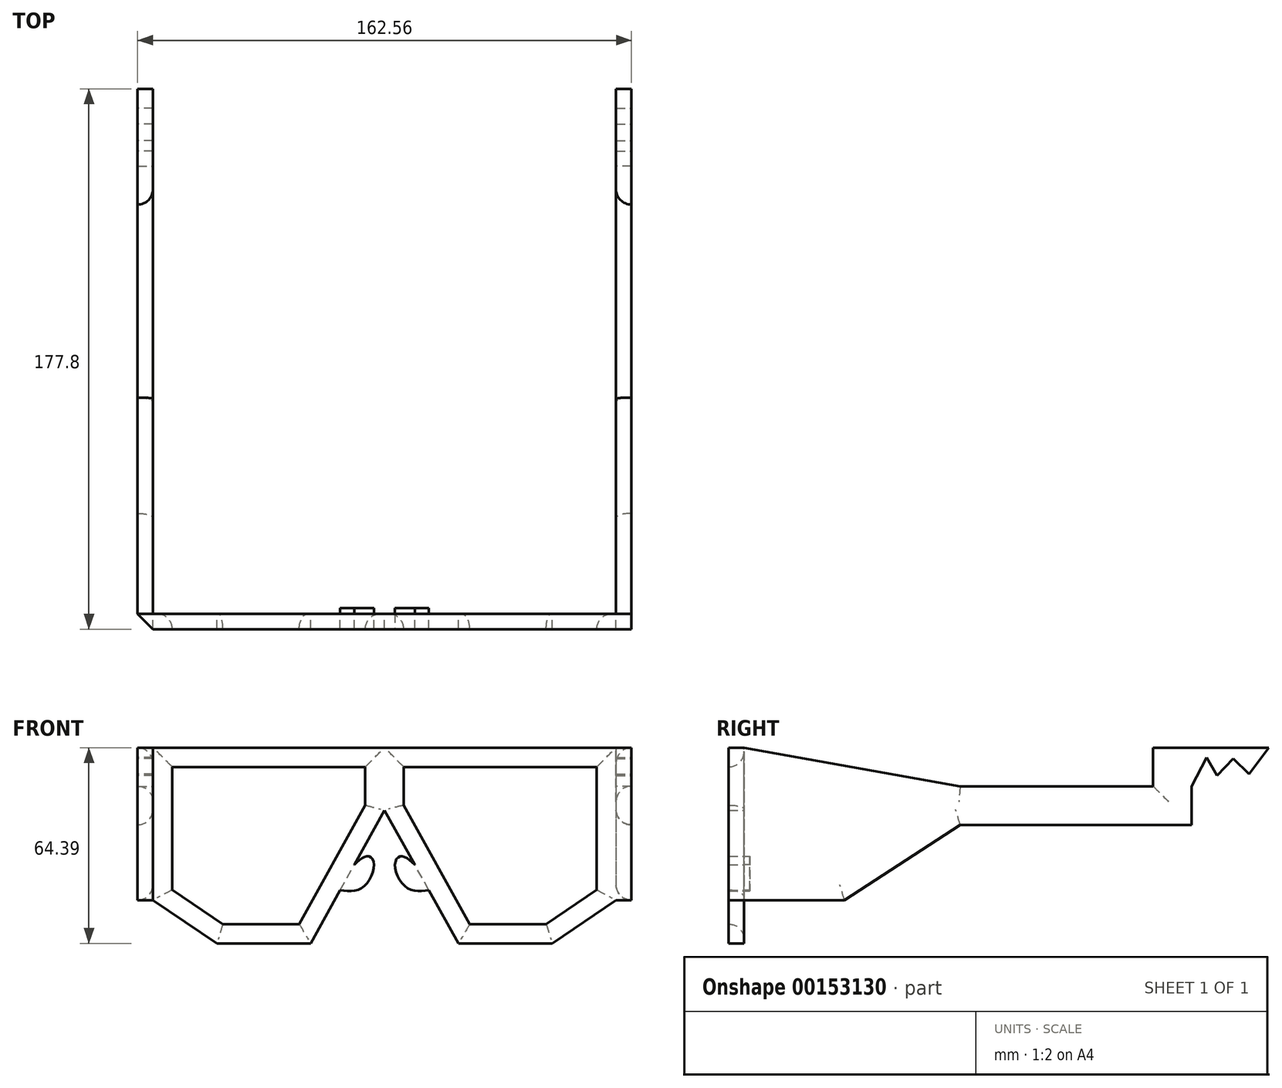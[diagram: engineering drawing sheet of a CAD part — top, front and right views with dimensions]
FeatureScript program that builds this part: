
annotation { "Feature Type Name" : "Feature", "Feature Type Description" : "" }
export const myFeature = defineFeature(function(context is Context, id is Id, definition is map)
    precondition{}
    {
        {
            var Q0;
            Q0=qCreatedBy(makeId("Front.planeOp"),FACE);
            var sketch = newSketch(context, id + "F0", { "sketchPlane" : qUnion([Q0])});
            skLineSegment(sketch, "E0", {"start": v(0, -20.57) * mm, "end": v(0, 0) * mm});
            skLineSegment(sketch, "E1", {"start": v(-76.2, 0) * mm, "end": v(-76.2, -50.16) * mm});
            skLineSegment(sketch, "E2", {"start": v(-76.2, -50.16) * mm, "end": v(-55.16, -64.4) * mm});
            skLineSegment(sketch, "E3", {"start": v(-55.16, -64.4) * mm, "end": v(-24.34, -64.4) * mm});
            skLineSegment(sketch, "E4", {"start": v(-24.34, -64.4) * mm, "end": v(0, -20.57) * mm});
            skLineSegment(sketch, "E5", {"start": v(-76.2, 0) * mm, "end": v(0, 0) * mm});
            skLineSegment(sketch, "E6.0", {"start": v(-53.22, -58.04) * mm, "end": v(-28.08, -58.04) * mm});
            skLineSegment(sketch, "E6.1", {"start": v(-6.35, -18.92) * mm, "end": v(-6.35, -6.35) * mm});
            skLineSegment(sketch, "E6.2", {"start": v(-69.85, -6.35) * mm, "end": v(-6.35, -6.35) * mm});
            skLineSegment(sketch, "E6.3", {"start": v(-28.08, -58.04) * mm, "end": v(-6.35, -18.92) * mm});
            skLineSegment(sketch, "E6.4", {"start": v(-69.85, -6.35) * mm, "end": v(-69.85, -46.79) * mm});
            skLineSegment(sketch, "E6.5", {"start": v(-69.85, -46.79) * mm, "end": v(-53.22, -58.04) * mm});
            skLineSegment(sketch, "E7.MirrorCS", {"start": v(69.85, -6.35) * mm, "end": v(6.35, -6.35) * mm});
            skLineSegment(sketch, "E8.MirrorCS", {"start": v(69.85, -46.79) * mm, "end": v(53.22, -58.04) * mm});
            skLineSegment(sketch, "E9.MirrorCS", {"start": v(24.34, -64.4) * mm, "end": v(0, -20.57) * mm});
            skLineSegment(sketch, "E10.MirrorCS", {"start": v(76.2, 0) * mm, "end": v(76.2, -50.16) * mm});
            skLineSegment(sketch, "E11.MirrorCS", {"start": v(28.08, -58.04) * mm, "end": v(6.35, -18.92) * mm});
            skLineSegment(sketch, "E12.MirrorCS", {"start": v(76.2, 0) * mm, "end": v(0, 0) * mm});
            skLineSegment(sketch, "E13.MirrorCS", {"start": v(6.35, -18.92) * mm, "end": v(6.35, -6.35) * mm});
            skLineSegment(sketch, "E14.MirrorCS", {"start": v(76.2, -50.16) * mm, "end": v(55.16, -64.4) * mm});
            skLineSegment(sketch, "E15.MirrorCS", {"start": v(53.22, -58.04) * mm, "end": v(28.08, -58.04) * mm});
            skLineSegment(sketch, "E16.MirrorCS", {"start": v(69.85, -6.35) * mm, "end": v(69.85, -46.79) * mm});
            skLineSegment(sketch, "E17.MirrorCS", {"start": v(55.16, -64.4) * mm, "end": v(24.34, -64.4) * mm});
            skSolve(sketch);
        }
        {
            var Q0;
            Q0=makeQuery(id+"F0.imprint","IMPRINT",FACE,{"disambiguationData":[TD([[makeQuery(id+"F0.imprint","IMPRINT",EDGE,{"derivedFrom":sQuery(id+"F0.wireOp",EDGE,"fyhn3gBe-UPRQ-DnYD-ZcEh-rTQ5N5aMUXou")}),1.0]])]});
            var Q1;
            Q1=makeQuery(id+"F0.imprint","IMPRINT",FACE,{"disambiguationData":[TD([[makeQuery(id+"F0.imprint","IMPRINT",EDGE,{"derivedFrom":sQuery(id+"F0.wireOp",EDGE,"FnI6rPoV-1xO5-tsXu-1lt8-hUfCxYtGt8Qp")}),-1.0]])]});
            var Q2;
            Q2=makeQuery(id+"F0.imprint","IMPRINT",FACE,{"disambiguationData":[TD([[makeQuery(id+"F0.imprint","IMPRINT",EDGE,{"derivedFrom":sQuery(id+"F0.wireOp",EDGE,"958f7f59-854b-43ef-8d78-6e4da16b072b5.MirrorCS")}),-1.0]])]});
            var Q3;
            Q3=makeQuery(id+"F0.imprint","IMPRINT",FACE,{"disambiguationData":[TD([[makeQuery(id+"F0.imprint","IMPRINT",EDGE,{"derivedFrom":sQuery(id+"F0.wireOp",EDGE,"958f7f59-854b-43ef-8d78-6e4da16b072b7.MirrorCS")}),-1.0]])]});
            var Q4;
            Q4=makeQuery(id+"F0.imprint","IMPRINT",FACE,{"disambiguationData":[TD([[makeQuery(id+"F0.imprint","IMPRINT",EDGE,{"derivedFrom":sQuery(id+"F0.wireOp",EDGE,"E0")}),-1.0]])]});
            var Q5;
            Q5=makeQuery(id+"F0.imprint","IMPRINT",FACE,{"disambiguationData":[TD([[makeQuery(id+"F0.imprint","IMPRINT",EDGE,{"derivedFrom":sQuery(id+"F0.wireOp",EDGE,"E0")}),1.0]])]});
            extrude(context, id + "F1", {"entities" : qUnion([Q0, Q1, Q2, Q3, Q4, Q5]), "depth" : 5.08 * mm});
        }
        {
            var Q0;
            Q0=makeQuery(id+"F1.opExtrude","SWEPT_FACE",FACE,{"disambiguationData":[OSD([sQuery(id+"F0.wireOp",EDGE,"E10.MirrorCS")])]});
            var sketch = newSketch(context, id + "F2", { "sketchPlane" : qUnion([Q0])});
            skLineSegment(sketch, "E18.0", {"start": v(-5.08, 0) * mm, "end": v(-5.08, -50.16) * mm});
            skLineSegment(sketch, "E19", {"start": v(-5.08, 0) * mm, "end": v(-5.08, -12.7) * mm});
            skLineSegment(sketch, "E20", {"start": v(-5.08, -12.7) * mm, "end": v(147.32, -12.7) * mm});
            skLineSegment(sketch, "E21", {"start": v(147.32, -12.7) * mm, "end": v(147.32, -25.4) * mm});
            skLineSegment(sketch, "E22", {"start": v(147.32, -25.4) * mm, "end": v(-5.08, -25.4) * mm});
            skLineSegment(sketch, "E23", {"start": v(-5.08, -25.4) * mm, "end": v(-5.08, -12.7) * mm});
            skSolve(sketch);
        }
        {
            var Q0;
            {var subQ0=sQuery(id+"F2.wireOp",EDGE,"E21");Q0=makeQuery(id+"F2.imprint","IMPRINT",FACE,{"disambiguationData":[TD([[makeQuery(id+"F2.imprint","IMPRINT",EDGE,{"derivedFrom":subQ0}),-1.0]])]});}
            var Q1;
            {var subQ0=sQuery(id+"F2.wireOp",EDGE,"E23");Q1=makeQuery(id+"F2.imprint","IMPRINT",FACE,{"disambiguationData":[TD([[makeQuery(id+"F2.imprint","IMPRINT",EDGE,{"derivedFrom":subQ0}),1.0]])]});}
            extrude(context, id + "F3", {"entities" : qUnion([Q0, Q1]), "operationType" : NewBodyOperationType.ADD, "depth" : 5.08 * mm});
        }
        {
            var Q0;
            Q0=makeQuery(id+"F1.opExtrude","SWEPT_FACE",FACE,{"disambiguationData":[OSD([sQuery(id+"F0.wireOp",EDGE,"E1")])]});
            var sketch = newSketch(context, id + "F4", { "sketchPlane" : qUnion([Q0])});
            skLineSegment(sketch, "E24.2", {"start": v(-147.32, -12.7) * mm, "end": v(-147.32, -25.4) * mm});
            skLineSegment(sketch, "E25", {"start": v(5.08, -12.7) * mm, "end": v(5.08, -25.4) * mm});
            skLineSegment(sketch, "E26", {"start": v(-147.32, -12.7) * mm, "end": v(5.08, -12.7) * mm});
            skLineSegment(sketch, "E27", {"start": v(5.08, -25.4) * mm, "end": v(-147.32, -25.4) * mm});
            skSolve(sketch);
        }
        {
            var Q0;
            {var subQ0=sQuery(id+"F4.wireOp",EDGE,"E24.2");Q0=makeQuery(id+"F4.imprint","IMPRINT",FACE,{"disambiguationData":[TD([[makeQuery(id+"F4.imprint","IMPRINT",EDGE,{"derivedFrom":subQ0}),1.0]])]});}
            var Q1;
            {var subQ0=sQuery(id+"F4.wireOp",EDGE,"E25");Q1=makeQuery(id+"F4.imprint","IMPRINT",FACE,{"disambiguationData":[TD([[makeQuery(id+"F4.imprint","IMPRINT",EDGE,{"derivedFrom":subQ0}),-1.0]])]});}
            extrude(context, id + "F5", {"entities" : qUnion([Q0, Q1]), "operationType" : NewBodyOperationType.ADD, "depth" : 5.08 * mm});
        }
        {
            var Q0;
            Q0=makeQuery(id+"F5.opExtrude","CAP_FACE",FACE,{"disambiguationData":[OSD([sQuery(id+"F4.wireOp",EDGE,"E24.2"),sQuery(id+"F4.wireOp",EDGE,"E25"),sQuery(id+"F4.wireOp",EDGE,"E26"),sQuery(id+"F4.wireOp",EDGE,"E27")])],"isStart":false});
            var sketch = newSketch(context, id + "F6", { "sketchPlane" : qUnion([Q0])});
            skLineSegment(sketch, "E28", {"start": v(-147.32, -12.7) * mm, "end": v(-134.62, -12.7) * mm});
            skLineSegment(sketch, "E29", {"start": v(-134.62, -12.7) * mm, "end": v(-134.62, 0) * mm});
            skLineSegment(sketch, "E30", {"start": v(-134.62, 0) * mm, "end": v(-172.72, 0) * mm});
            skLineSegment(sketch, "E31", {"start": v(-172.72, 0) * mm, "end": v(-166.27, -8.63) * mm});
            skLineSegment(sketch, "E32", {"start": v(-166.27, -8.63) * mm, "end": v(-161.06, -3.6) * mm});
            skLineSegment(sketch, "E33", {"start": v(-161.06, -3.6) * mm, "end": v(-155.7, -9.17) * mm});
            skLineSegment(sketch, "E34", {"start": v(-155.7, -9.17) * mm, "end": v(-152.26, -3.24) * mm});
            skLineSegment(sketch, "E35", {"start": v(-152.26, -3.24) * mm, "end": v(-147.32, -12.7) * mm});
            skSolve(sketch);
        }
        {
            var Q0;
            Q0=makeQuery(id+"F6.imprint","IMPRINT",FACE,{"disambiguationData":[TD([[makeQuery(id+"F6.imprint","IMPRINT",EDGE,{"derivedFrom":sQuery(id+"F6.wireOp",EDGE,"E28")}),1.0]])]});
            var Q1;
            Q1=makeQuery(id+"F5.opExtrude","CAP_FACE",FACE,{"disambiguationData":[OSD([sQuery(id+"F4.wireOp",EDGE,"E24.2"),sQuery(id+"F4.wireOp",EDGE,"E25"),sQuery(id+"F4.wireOp",EDGE,"E26"),sQuery(id+"F4.wireOp",EDGE,"E27")])],"isStart":true});
            extrude(context, id + "F7", {"entities" : qUnion([Q0]), "operationType" : NewBodyOperationType.ADD, "endBound" : BoundingType.UP_TO_SURFACE, "oppositeDirection" : true, "endBoundEntityFace" : qUnion([Q1]), "depth" : 25.4 * mm});
        }
        {
            var Q0;
            Q0=makeQuery(id+"F3.opExtrude","CAP_FACE",FACE,{"disambiguationData":[OSD([sQuery(id+"F2.wireOp",EDGE,"E20"),sQuery(id+"F2.wireOp",EDGE,"E21"),sQuery(id+"F2.wireOp",EDGE,"E22"),sQuery(id+"F2.wireOp",EDGE,"E23")])],"isStart":false});
            var sketch = newSketch(context, id + "F8", { "sketchPlane" : qUnion([Q0])});
            skLineSegment(sketch, "E36.0", {"start": v(134.62, 0) * mm, "end": v(134.62, -12.7) * mm});
            skLineSegment(sketch, "E36.1", {"start": v(172.72, 0) * mm, "end": v(134.62, 0) * mm});
            skLineSegment(sketch, "E36.2", {"start": v(147.32, -12.7) * mm, "end": v(152.26, -3.24) * mm});
            skLineSegment(sketch, "E36.3", {"start": v(152.26, -3.24) * mm, "end": v(155.7, -9.17) * mm});
            skLineSegment(sketch, "E36.4", {"start": v(155.7, -9.17) * mm, "end": v(161.06, -3.6) * mm});
            skLineSegment(sketch, "E36.5", {"start": v(161.06, -3.6) * mm, "end": v(166.27, -8.63) * mm});
            skLineSegment(sketch, "E36.6", {"start": v(166.27, -8.63) * mm, "end": v(172.72, 0) * mm});
            skLineSegment(sketch, "E36.7", {"start": v(-5.08, -12.7) * mm, "end": v(147.32, -12.7) * mm});
            skSolve(sketch);
        }
        {
            var Q0;
            {var subQ1=sQuery(id+"F8.wireOp",EDGE,"E36.0");Q0=makeQuery(id+"F8.imprint","IMPRINT",FACE,{"disambiguationData":[TD([[makeQuery(id+"F8.imprint","IMPRINT",EDGE,{"derivedFrom":subQ1}),1.0]])]});}
            var Q1;
            Q1=makeQuery(id+"F3.opExtrude","CAP_FACE",FACE,{"disambiguationData":[OSD([sQuery(id+"F2.wireOp",EDGE,"E20"),sQuery(id+"F2.wireOp",EDGE,"E21"),sQuery(id+"F2.wireOp",EDGE,"E22"),sQuery(id+"F2.wireOp",EDGE,"E23")])],"isStart":true});
            extrude(context, id + "F9", {"entities" : qUnion([Q0]), "operationType" : NewBodyOperationType.ADD, "endBound" : BoundingType.UP_TO_SURFACE, "oppositeDirection" : true, "endBoundEntityFace" : qUnion([Q1]), "depth" : 25.4 * mm});
        }
        {
            var Q0;
            Q0=makeQuery(id+"F9.boolean.opBoolean","MERGE",FACE,{"derivedFrom":[makeQuery(id+"F3.opExtrude","CAP_FACE",FACE,{"disambiguationData":[OSD([sQuery(id+"F2.wireOp",EDGE,"E20"),sQuery(id+"F2.wireOp",EDGE,"E21"),sQuery(id+"F2.wireOp",EDGE,"E22"),sQuery(id+"F2.wireOp",EDGE,"E23")])],"isStart":false}),makeQuery(id+"F9.opExtrude","CAP_FACE",FACE,{"disambiguationData":[OSD([sQuery(id+"F8.wireOp",EDGE,"E36.0"),sQuery(id+"F8.wireOp",EDGE,"E36.1"),sQuery(id+"F8.wireOp",EDGE,"E36.2"),sQuery(id+"F8.wireOp",EDGE,"E36.3"),sQuery(id+"F8.wireOp",EDGE,"E36.4"),sQuery(id+"F8.wireOp",EDGE,"E36.5"),sQuery(id+"F8.wireOp",EDGE,"E36.6"),sQuery(id+"F8.wireOp",EDGE,"E36.7")])],"isStart":true})]});
            var sketch = newSketch(context, id + "F10", { "sketchPlane" : qUnion([Q0])});
            skLineSegment(sketch, "E37.0", {"start": v(-5.08, -12.7) * mm, "end": v(-5.08, -25.4) * mm});
            skLineSegment(sketch, "E37.1", {"start": v(-5.08, 0) * mm, "end": v(-5.08, -12.7) * mm});
            skLineSegment(sketch, "E37.2", {"start": v(-5.08, -25.4) * mm, "end": v(-5.08, -50.16) * mm});
            skLineSegment(sketch, "E38", {"start": v(-5.08, -50.16) * mm, "end": v(33.02, -50.16) * mm});
            skLineSegment(sketch, "E39", {"start": v(33.02, -50.16) * mm, "end": v(71.12, -25.4) * mm});
            skLineSegment(sketch, "E40", {"start": v(71.12, -25.4) * mm, "end": v(71.12, -12.7) * mm});
            skLineSegment(sketch, "E41", {"start": v(-5.08, 0) * mm, "end": v(0, 0) * mm});
            skLineSegment(sketch, "E42", {"start": v(0, 0) * mm, "end": v(71.12, -12.7) * mm});
            skSolve(sketch);
        }
        {
            var Q0;
            {var subQ0=sQuery(id+"F10.wireOp",EDGE,"E37.2");Q0=makeQuery(id+"F10.imprint","IMPRINT",FACE,{"disambiguationData":[TD([[makeQuery(id+"F10.imprint","IMPRINT",EDGE,{"derivedFrom":subQ0}),1.0]])]});}
            var Q1;
            {var subQ0=sQuery(id+"F10.wireOp",EDGE,"E37.1");Q1=makeQuery(id+"F10.imprint","IMPRINT",FACE,{"disambiguationData":[TD([[makeQuery(id+"F10.imprint","IMPRINT",EDGE,{"derivedFrom":subQ0}),1.0]])]});}
            var Q2;
            Q2=makeQuery(id+"F9.boolean.opBoolean","MERGE",FACE,{"derivedFrom":[makeQuery(id+"F3.opExtrude","CAP_FACE",FACE,{"disambiguationData":[OSD([sQuery(id+"F2.wireOp",EDGE,"E20"),sQuery(id+"F2.wireOp",EDGE,"E21"),sQuery(id+"F2.wireOp",EDGE,"E22"),sQuery(id+"F2.wireOp",EDGE,"E23")])],"isStart":true}),makeQuery(id+"F9.opExtrude","CAP_FACE",FACE,{"disambiguationData":[OSD([sQuery(id+"F8.wireOp",EDGE,"E36.0"),sQuery(id+"F8.wireOp",EDGE,"E36.1"),sQuery(id+"F8.wireOp",EDGE,"E36.2"),sQuery(id+"F8.wireOp",EDGE,"E36.3"),sQuery(id+"F8.wireOp",EDGE,"E36.4"),sQuery(id+"F8.wireOp",EDGE,"E36.5"),sQuery(id+"F8.wireOp",EDGE,"E36.6"),sQuery(id+"F8.wireOp",EDGE,"E36.7")])],"isStart":false})]});
            extrude(context, id + "F11", {"entities" : qUnion([Q0, Q1]), "operationType" : NewBodyOperationType.ADD, "endBound" : BoundingType.UP_TO_SURFACE, "oppositeDirection" : true, "endBoundEntityFace" : qUnion([Q2]), "depth" : 25.4 * mm});
        }
        {
            var Q0;
            Q0=makeQuery(id+"F7.boolean.opBoolean","MERGE",FACE,{"derivedFrom":[makeQuery(id+"F5.opExtrude","CAP_FACE",FACE,{"disambiguationData":[OSD([sQuery(id+"F4.wireOp",EDGE,"E24.2"),sQuery(id+"F4.wireOp",EDGE,"E25"),sQuery(id+"F4.wireOp",EDGE,"E26"),sQuery(id+"F4.wireOp",EDGE,"E27")])],"isStart":false}),makeQuery(id+"F7.opExtrude","CAP_FACE",FACE,{"disambiguationData":[OSD([sQuery(id+"F6.wireOp",EDGE,"E28"),sQuery(id+"F6.wireOp",EDGE,"E29"),sQuery(id+"F6.wireOp",EDGE,"E30"),sQuery(id+"F6.wireOp",EDGE,"E31"),sQuery(id+"F6.wireOp",EDGE,"E32"),sQuery(id+"F6.wireOp",EDGE,"E33"),sQuery(id+"F6.wireOp",EDGE,"E34"),sQuery(id+"F6.wireOp",EDGE,"E35")])],"isStart":true})]});
            var sketch = newSketch(context, id + "F12", { "sketchPlane" : qUnion([Q0])});
            skLineSegment(sketch, "E43.0", {"start": v(-33.02, -50.16) * mm, "end": v(0, -50.16) * mm});
            skLineSegment(sketch, "E43.1", {"start": v(5.08, -50.16) * mm, "end": v(0, -50.16) * mm});
            skLineSegment(sketch, "E43.2", {"start": v(-71.12, -25.4) * mm, "end": v(-33.02, -50.16) * mm});
            skLineSegment(sketch, "E43.3", {"start": v(-71.12, -12.7) * mm, "end": v(0, 0) * mm});
            skLineSegment(sketch, "E43.4", {"start": v(5.08, 0) * mm, "end": v(0, 0) * mm});
            skLineSegment(sketch, "E43.5", {"start": v(5.08, 0) * mm, "end": v(5.08, -12.7) * mm});
            skLineSegment(sketch, "E43.6", {"start": v(5.08, -12.7) * mm, "end": v(5.08, -25.4) * mm});
            skLineSegment(sketch, "E43.7", {"start": v(5.08, -25.4) * mm, "end": v(5.08, -50.16) * mm});
            skLineSegment(sketch, "E44", {"start": v(-71.12, -12.7) * mm, "end": v(-71.12, -25.4) * mm});
            skSolve(sketch);
        }
        {
            var Q0;
            {var subQ0=sQuery(id+"F12.wireOp",EDGE,"E43.3");Q0=makeQuery(id+"F12.imprint","IMPRINT",FACE,{"disambiguationData":[TD([[makeQuery(id+"F12.imprint","IMPRINT",EDGE,{"derivedFrom":subQ0}),-1.0]])]});}
            var Q1;
            Q1=makeQuery(id+"F12.imprint","IMPRINT",FACE,{"disambiguationData":[TD([[makeQuery(id+"F12.imprint","IMPRINT",EDGE,{"derivedFrom":sQuery(id+"F12.wireOp",EDGE,"E43.0")}),1.0]])]});
            var Q2;
            Q2=makeQuery(id+"F7.boolean.opBoolean","MERGE",FACE,{"derivedFrom":[makeQuery(id+"F5.opExtrude","CAP_FACE",FACE,{"disambiguationData":[OSD([sQuery(id+"F4.wireOp",EDGE,"E24.2"),sQuery(id+"F4.wireOp",EDGE,"E25"),sQuery(id+"F4.wireOp",EDGE,"E26"),sQuery(id+"F4.wireOp",EDGE,"E27")])],"isStart":true}),makeQuery(id+"F7.opExtrude","CAP_FACE",FACE,{"disambiguationData":[OSD([sQuery(id+"F6.wireOp",EDGE,"E28"),sQuery(id+"F6.wireOp",EDGE,"E29"),sQuery(id+"F6.wireOp",EDGE,"E30"),sQuery(id+"F6.wireOp",EDGE,"E31"),sQuery(id+"F6.wireOp",EDGE,"E32"),sQuery(id+"F6.wireOp",EDGE,"E33"),sQuery(id+"F6.wireOp",EDGE,"E34"),sQuery(id+"F6.wireOp",EDGE,"E35")])],"isStart":false})]});
            extrude(context, id + "F13", {"entities" : qUnion([Q0, Q1]), "operationType" : NewBodyOperationType.ADD, "endBound" : BoundingType.UP_TO_SURFACE, "oppositeDirection" : true, "endBoundEntityFace" : qUnion([Q2]), "depth" : 25.4 * mm});
        }
        {
            var Q0;
            Q0=makeQuery(id+"F13.boolean.opBoolean","MERGE",EDGE,{"derivedFrom":[makeQuery(id+"F5.opExtrude","CAP_EDGE",EDGE,{"disambiguationData":[OSD([sQuery(id+"F4.wireOp",EDGE,"E25")])],"isStart":false}),makeQuery(id+"F13.opExtrude","CAP_EDGE",EDGE,{"disambiguationData":[OSD([sQuery(id+"F12.wireOp",EDGE,"E43.5")])],"isStart":true}),makeQuery(id+"F13.opExtrude","CAP_EDGE",EDGE,{"disambiguationData":[OSD([sQuery(id+"F12.wireOp",EDGE,"E43.7")])],"isStart":true})]});
            var Q1;
            Q1=makeQuery(id+"F11.boolean.opBoolean","MERGE",EDGE,{"derivedFrom":[makeQuery(id+"F3.opExtrude","CAP_EDGE",EDGE,{"disambiguationData":[OSD([sQuery(id+"F2.wireOp",EDGE,"E23")])],"isStart":false}),makeQuery(id+"F11.opExtrude","CAP_EDGE",EDGE,{"disambiguationData":[OSD([sQuery(id+"F10.wireOp",EDGE,"E37.1")])],"isStart":true}),makeQuery(id+"F11.opExtrude","CAP_EDGE",EDGE,{"disambiguationData":[OSD([sQuery(id+"F10.wireOp",EDGE,"E37.2")])],"isStart":true})]});
            chamfer(context, id + "F14", {"entities" : qUnion([Q0, Q1]), "width" : 5.08 * mm, "tangentPropagation" : true});
        }
        {
            var Q0;
            Q0=makeQuery(id+"F11.opExtrude","CAP_EDGE",EDGE,{"disambiguationData":[OSD([sQuery(id+"F10.wireOp",EDGE,"E39")])],"isStart":false});
            var Q1;
            Q1=makeQuery(id+"F11.boolean.opBoolean","SPLIT",EDGE,{"derivedFrom":makeQuery(id+"F11.opExtrude","CAP_EDGE",EDGE,{"disambiguationData":[OSD([sQuery(id+"F10.wireOp",EDGE,"E38")])],"isStart":false})});
            var Q2;
            {var subQ0=sQuery(id+"F2.wireOp",EDGE,"E21");var subQ1=sQuery(id+"F2.wireOp",EDGE,"E22");Q2=makeQuery(id+"F3.boolean.opBoolean","SPLIT",EDGE,{"disambiguationData":[TD([makeQuery(id+"F3.opExtrude","SWEPT_FACE",FACE,{"disambiguationData":[OSD([subQ0])]})])],"derivedFrom":makeQuery(id+"F3.opExtrude","CAP_EDGE",EDGE,{"disambiguationData":[OSD([subQ1])],"isStart":true})});}
            var Q3;
            {var subQ0=sQuery(id+"F2.wireOp",EDGE,"E21");var subQ1=sQuery(id+"F2.wireOp",EDGE,"E20");Q3=makeQuery(id+"F3.boolean.opBoolean","SPLIT",EDGE,{"disambiguationData":[TD([makeQuery(id+"F3.opExtrude","SWEPT_FACE",FACE,{"disambiguationData":[OSD([subQ0])]})])],"derivedFrom":makeQuery(id+"F3.opExtrude","CAP_EDGE",EDGE,{"disambiguationData":[OSD([subQ1])],"isStart":true})});}
            var Q4;
            Q4=makeQuery(id+"F11.opExtrude","CAP_EDGE",EDGE,{"disambiguationData":[OSD([sQuery(id+"F10.wireOp",EDGE,"E42")])],"isStart":false});
            var Q5;
            Q5=makeQuery(id+"F9.opExtrude","CAP_EDGE",EDGE,{"disambiguationData":[OSD([sQuery(id+"F8.wireOp",EDGE,"E36.0")])],"isStart":false});
            fillet(context, id + "F15", {"entities" : qUnion([Q0, Q1, Q2, Q3, Q4, Q5]), "radius" : 5.08 * mm, "tangentPropagation" : true, "allowEdgeOverflow" : false});
        }
        {
            var Q0;
            Q0=makeQuery(id+"F13.opExtrude","CAP_EDGE",EDGE,{"disambiguationData":[OSD([sQuery(id+"F12.wireOp",EDGE,"E43.3")])],"isStart":false});
            var Q1;
            {var subQ0=sQuery(id+"F4.wireOp",EDGE,"E26");var subQ1=sQuery(id+"F4.wireOp",EDGE,"E24.2");Q1=makeQuery(id+"F5.boolean.opBoolean","SPLIT",EDGE,{"disambiguationData":[TD([makeQuery(id+"F5.opExtrude","SWEPT_FACE",FACE,{"disambiguationData":[OSD([subQ1])]})])],"derivedFrom":makeQuery(id+"F5.opExtrude","CAP_EDGE",EDGE,{"disambiguationData":[OSD([subQ0])],"isStart":true})});}
            var Q2;
            {var subQ0=sQuery(id+"F4.wireOp",EDGE,"E27");var subQ1=sQuery(id+"F4.wireOp",EDGE,"E24.2");Q2=makeQuery(id+"F5.boolean.opBoolean","SPLIT",EDGE,{"disambiguationData":[TD([makeQuery(id+"F5.opExtrude","SWEPT_FACE",FACE,{"disambiguationData":[OSD([subQ1])]})])],"derivedFrom":makeQuery(id+"F5.opExtrude","CAP_EDGE",EDGE,{"disambiguationData":[OSD([subQ0])],"isStart":true})});}
            var Q3;
            Q3=makeQuery(id+"F13.opExtrude","CAP_EDGE",EDGE,{"disambiguationData":[OSD([sQuery(id+"F12.wireOp",EDGE,"E43.2")])],"isStart":false});
            var Q4;
            Q4=makeQuery(id+"F13.boolean.opBoolean","SPLIT",EDGE,{"derivedFrom":makeQuery(id+"F13.opExtrude","CAP_EDGE",EDGE,{"disambiguationData":[OSD([sQuery(id+"F12.wireOp",EDGE,"E43.0"),sQuery(id+"F12.wireOp",EDGE,"E43.1")])],"isStart":false})});
            var Q5;
            Q5=makeQuery(id+"F7.opExtrude","CAP_EDGE",EDGE,{"disambiguationData":[OSD([sQuery(id+"F6.wireOp",EDGE,"E29")])],"isStart":false});
            fillet(context, id + "F16", {"entities" : qUnion([Q0, Q1, Q2, Q3, Q4, Q5]), "radius" : 5.08 * mm, "tangentPropagation" : true, "allowEdgeOverflow" : false});
        }
        {
            var Q0;
            Q0=makeQuery(id+"F1.opExtrude","CAP_EDGE",EDGE,{"disambiguationData":[OSD([sQuery(id+"F0.wireOp",EDGE,"E6.3")])],"isStart":true});
            var Q1;
            Q1=makeQuery(id+"F1.opExtrude","CAP_EDGE",EDGE,{"disambiguationData":[OSD([sQuery(id+"F0.wireOp",EDGE,"E6.1")])],"isStart":true});
            var Q2;
            Q2=makeQuery(id+"F1.opExtrude","CAP_EDGE",EDGE,{"disambiguationData":[OSD([sQuery(id+"F0.wireOp",EDGE,"E6.2")])],"isStart":true});
            var Q3;
            Q3=makeQuery(id+"F1.opExtrude","CAP_EDGE",EDGE,{"disambiguationData":[OSD([sQuery(id+"F0.wireOp",EDGE,"E6.4")])],"isStart":true});
            var Q4;
            Q4=makeQuery(id+"F1.opExtrude","CAP_EDGE",EDGE,{"disambiguationData":[OSD([sQuery(id+"F0.wireOp",EDGE,"E6.5")])],"isStart":true});
            var Q5;
            Q5=makeQuery(id+"F1.opExtrude","CAP_EDGE",EDGE,{"disambiguationData":[OSD([sQuery(id+"F0.wireOp",EDGE,"E6.0")])],"isStart":true});
            var Q6;
            Q6=makeQuery(id+"F1.opExtrude","CAP_EDGE",EDGE,{"disambiguationData":[OSD([sQuery(id+"F0.wireOp",EDGE,"E11.MirrorCS")])],"isStart":true});
            var Q7;
            Q7=makeQuery(id+"F1.opExtrude","CAP_EDGE",EDGE,{"disambiguationData":[OSD([sQuery(id+"F0.wireOp",EDGE,"E13.MirrorCS")])],"isStart":true});
            var Q8;
            Q8=makeQuery(id+"F1.opExtrude","CAP_EDGE",EDGE,{"disambiguationData":[OSD([sQuery(id+"F0.wireOp",EDGE,"E7.MirrorCS")])],"isStart":true});
            var Q9;
            Q9=makeQuery(id+"F1.opExtrude","CAP_EDGE",EDGE,{"disambiguationData":[OSD([sQuery(id+"F0.wireOp",EDGE,"E16.MirrorCS")])],"isStart":true});
            var Q10;
            Q10=makeQuery(id+"F1.opExtrude","CAP_EDGE",EDGE,{"disambiguationData":[OSD([sQuery(id+"F0.wireOp",EDGE,"E8.MirrorCS")])],"isStart":true});
            var Q11;
            Q11=makeQuery(id+"F1.opExtrude","CAP_EDGE",EDGE,{"disambiguationData":[OSD([sQuery(id+"F0.wireOp",EDGE,"E15.MirrorCS")])],"isStart":true});
            fillet(context, id + "F17", {"entities" : qUnion([Q0, Q1, Q2, Q3, Q4, Q5, Q6, Q7, Q8, Q9, Q10, Q11]), "radius" : 5.08 * mm, "tangentPropagation" : true, "allowEdgeOverflow" : false});
        }
        {
            var Q0;
            Q0=makeQuery(id+"F1.opExtrude","CAP_FACE",FACE,{"disambiguationData":[OSD([sQuery(id+"F0.wireOp",EDGE,"E1"),sQuery(id+"F0.wireOp",EDGE,"E2"),sQuery(id+"F0.wireOp",EDGE,"E3"),sQuery(id+"F0.wireOp",EDGE,"E4"),sQuery(id+"F0.wireOp",EDGE,"E5"),sQuery(id+"F0.wireOp",EDGE,"E6.0"),sQuery(id+"F0.wireOp",EDGE,"E6.1"),sQuery(id+"F0.wireOp",EDGE,"E6.2"),sQuery(id+"F0.wireOp",EDGE,"E6.3"),sQuery(id+"F0.wireOp",EDGE,"E6.4"),sQuery(id+"F0.wireOp",EDGE,"E6.5"),sQuery(id+"F0.wireOp",EDGE,"E7.MirrorCS"),sQuery(id+"F0.wireOp",EDGE,"E8.MirrorCS"),sQuery(id+"F0.wireOp",EDGE,"E9.MirrorCS"),sQuery(id+"F0.wireOp",EDGE,"E10.MirrorCS"),sQuery(id+"F0.wireOp",EDGE,"E11.MirrorCS"),sQuery(id+"F0.wireOp",EDGE,"E12.MirrorCS"),sQuery(id+"F0.wireOp",EDGE,"E13.MirrorCS"),sQuery(id+"F0.wireOp",EDGE,"E14.MirrorCS"),sQuery(id+"F0.wireOp",EDGE,"E15.MirrorCS"),sQuery(id+"F0.wireOp",EDGE,"E16.MirrorCS"),sQuery(id+"F0.wireOp",EDGE,"E17.MirrorCS")])],"isStart":true});
            var sketch = newSketch(context, id + "F18", { "sketchPlane" : qUnion([Q0])});
            skFitSpline(sketch, "E45", {"points": [v(10, -38.55) * mm, v(5.54, -35.68) * mm, v(3.48, -38.04) * mm, v(7.2, -46.02) * mm, v(14.62, -46.9) * mm], "startDerivative": vector(-19.9, 18.49) * mm, "endDerivative": vector(28.38, 3.62) * mm});
            skFitSpline(sketch, "E46.MirrorCS", {"points": [v(-10, -38.55) * mm, v(-5.54, -35.68) * mm, v(-3.48, -38.04) * mm, v(-7.2, -46.02) * mm, v(-14.62, -46.9) * mm], "startDerivative": vector(19.9, 18.49) * mm, "endDerivative": vector(-28.38, 3.62) * mm});
            skSolve(sketch);
        }
        {
            var Q0;
            {var subQ0=sQuery(id+"F18.wireOp",EDGE,"E46.MirrorCS");Q0=makeQuery(id+"F18.imprint","IMPRINT",FACE,{"disambiguationData":[TD([[makeQuery(id+"F18.imprint","IMPRINT",EDGE,{"derivedFrom":subQ0}),-1.0]])]});}
            var Q1;
            {var subQ0=sQuery(id+"F18.wireOp",EDGE,"E45");Q1=makeQuery(id+"F18.imprint","IMPRINT",FACE,{"disambiguationData":[TD([[makeQuery(id+"F18.imprint","IMPRINT",EDGE,{"derivedFrom":subQ0}),1.0]])]});}
            var Q2;
            Q2=makeQuery(id+"F13.boolean.opBoolean","MERGE",FACE,{"derivedFrom":[makeQuery(id+"F11.boolean.opBoolean","MERGE",FACE,{"derivedFrom":[makeQuery(id+"F5.boolean.opBoolean","MERGE",FACE,{"derivedFrom":[makeQuery(id+"F3.boolean.opBoolean","MERGE",FACE,{"derivedFrom":[makeQuery(id+"F1.opExtrude","CAP_FACE",FACE,{"disambiguationData":[OSD([sQuery(id+"F0.wireOp",EDGE,"E1"),sQuery(id+"F0.wireOp",EDGE,"E2"),sQuery(id+"F0.wireOp",EDGE,"E3"),sQuery(id+"F0.wireOp",EDGE,"E4"),sQuery(id+"F0.wireOp",EDGE,"E5"),sQuery(id+"F0.wireOp",EDGE,"E6.0"),sQuery(id+"F0.wireOp",EDGE,"E6.1"),sQuery(id+"F0.wireOp",EDGE,"E6.2"),sQuery(id+"F0.wireOp",EDGE,"E6.3"),sQuery(id+"F0.wireOp",EDGE,"E6.4"),sQuery(id+"F0.wireOp",EDGE,"E6.5"),sQuery(id+"F0.wireOp",EDGE,"E7.MirrorCS"),sQuery(id+"F0.wireOp",EDGE,"E8.MirrorCS"),sQuery(id+"F0.wireOp",EDGE,"E9.MirrorCS"),sQuery(id+"F0.wireOp",EDGE,"E10.MirrorCS"),sQuery(id+"F0.wireOp",EDGE,"E11.MirrorCS"),sQuery(id+"F0.wireOp",EDGE,"E12.MirrorCS"),sQuery(id+"F0.wireOp",EDGE,"E13.MirrorCS"),sQuery(id+"F0.wireOp",EDGE,"E14.MirrorCS"),sQuery(id+"F0.wireOp",EDGE,"E15.MirrorCS"),sQuery(id+"F0.wireOp",EDGE,"E16.MirrorCS"),sQuery(id+"F0.wireOp",EDGE,"E17.MirrorCS")])],"isStart":false}),makeQuery(id+"F3.opExtrude","SWEPT_FACE",FACE,{"disambiguationData":[OSD([sQuery(id+"F2.wireOp",EDGE,"E23")])]})]}),makeQuery(id+"F5.opExtrude","SWEPT_FACE",FACE,{"disambiguationData":[OSD([sQuery(id+"F4.wireOp",EDGE,"E25")])]})]}),makeQuery(id+"F11.opExtrude","SWEPT_FACE",FACE,{"disambiguationData":[OSD([sQuery(id+"F10.wireOp",EDGE,"E37.1")])]}),makeQuery(id+"F11.opExtrude","SWEPT_FACE",FACE,{"disambiguationData":[OSD([sQuery(id+"F10.wireOp",EDGE,"E37.2")])]})]}),makeQuery(id+"F13.opExtrude","SWEPT_FACE",FACE,{"disambiguationData":[OSD([sQuery(id+"F12.wireOp",EDGE,"E43.5")])]}),makeQuery(id+"F13.opExtrude","SWEPT_FACE",FACE,{"disambiguationData":[OSD([sQuery(id+"F12.wireOp",EDGE,"E43.7")])]})]});
            extrude(context, id + "F19", {"entities" : qUnion([Q0, Q1]), "operationType" : NewBodyOperationType.ADD, "endBound" : BoundingType.UP_TO_SURFACE, "oppositeDirection" : true, "endBoundEntityFace" : qUnion([Q2]), "depth" : 5.7 * mm});
        }
        {
            var Q0;
            {var subQ0=sQuery(id+"F18.wireOp",EDGE,"E46.MirrorCS");Q0=makeQuery(id+"F18.imprint","IMPRINT",FACE,{"disambiguationData":[TD([[makeQuery(id+"F18.imprint","IMPRINT",EDGE,{"derivedFrom":subQ0}),-1.0]])]});}
            var Q1;
            {var subQ0=sQuery(id+"F18.wireOp",EDGE,"E45");Q1=makeQuery(id+"F18.imprint","IMPRINT",FACE,{"disambiguationData":[TD([[makeQuery(id+"F18.imprint","IMPRINT",EDGE,{"derivedFrom":subQ0}),1.0]])]});}
            extrude(context, id + "F20", {"entities" : qUnion([Q0, Q1]), "operationType" : NewBodyOperationType.ADD, "depth" : 1.9 * mm});
        }
    });
